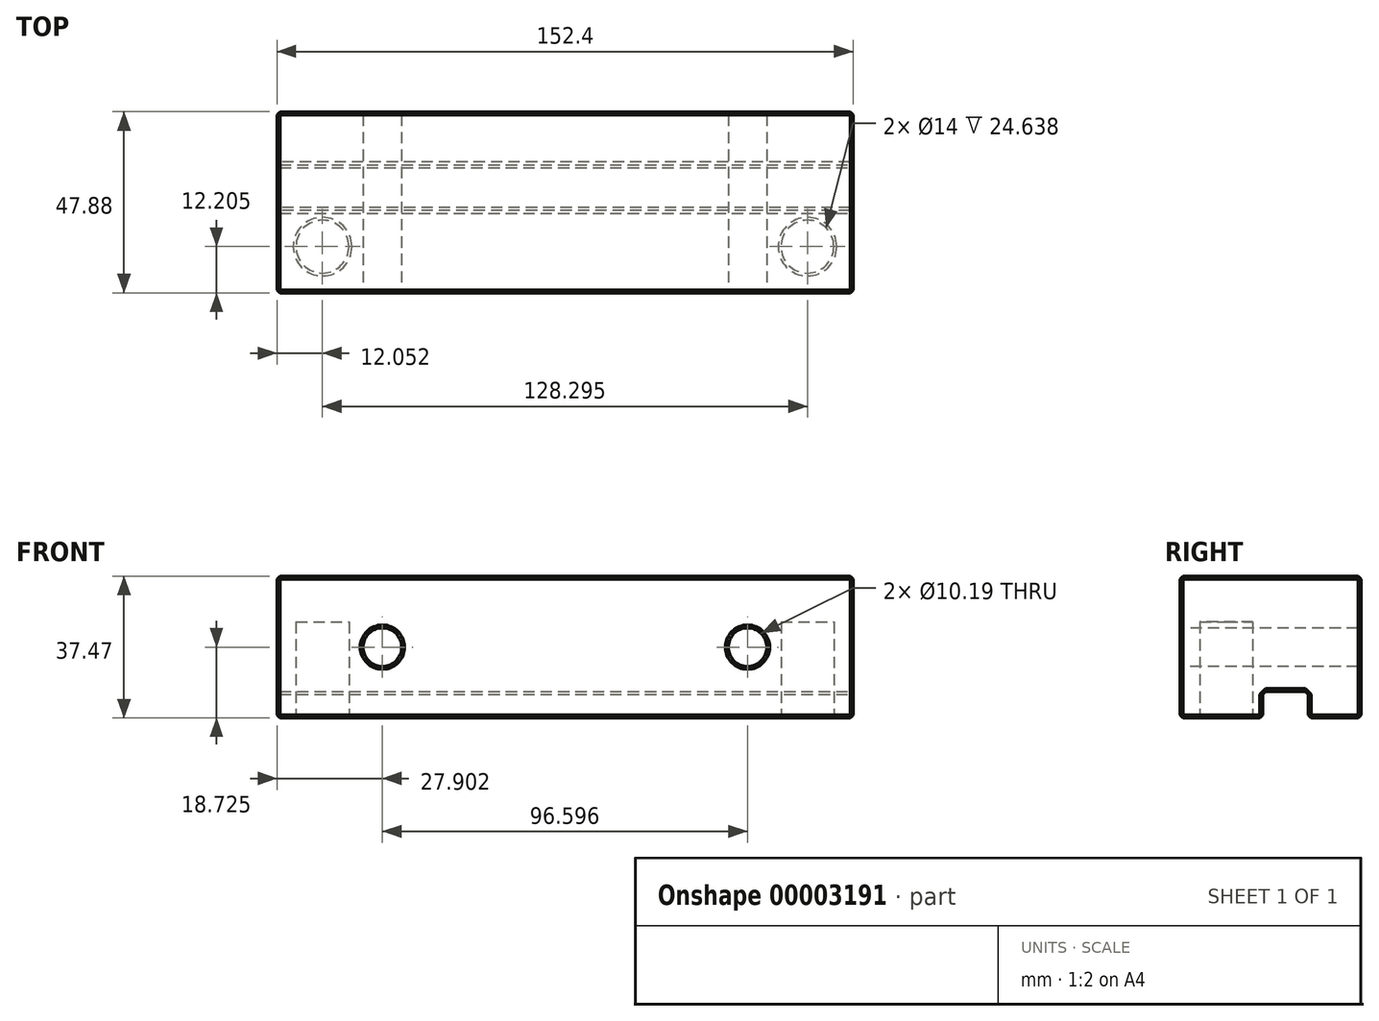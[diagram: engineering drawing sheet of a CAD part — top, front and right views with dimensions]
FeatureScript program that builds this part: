
annotation { "Feature Type Name" : "Feature", "Feature Type Description" : "" }
export const myFeature = defineFeature(function(context is Context, id is Id, definition is map)
    precondition{}
    {
        {
            var Q0;
            Q0=qCreatedBy(makeId("Front.planeOp"),FACE);
            var sketch = newSketch(context, id + "F0", { "sketchPlane" : qUnion([Q0])});
            skLineSegment(sketch, "E0.bottom", {"start": v(0, 0) * mm, "end": v(152.4, 0) * mm});
            skLineSegment(sketch, "E0.top", {"start": v(0, -37.47) * mm, "end": v(152.4, -37.47) * mm});
            skLineSegment(sketch, "E0.left", {"start": v(0, 0) * mm, "end": v(0, -37.47) * mm});
            skLineSegment(sketch, "E0.right", {"start": v(152.4, 0) * mm, "end": v(152.4, -37.47) * mm});
            skCircle(sketch, "E1", {"center": v(27.9, -18.75) * mm, "radius": 5.1 * mm});
            skCircle(sketch, "E2", {"center": v(124.5, -18.75) * mm, "radius": 5.1 * mm});
            skLineSegment(sketch, "E3", {"start": v(27.9, -18.75) * mm, "end": v(124.5, -18.75) * mm, "construction": true});
            skPoint(sketch, "E4", {"position": v(76.2, -18.75) * mm});
            skSolve(sketch);
        }
        {
            var Q0;
            Q0 = qSketchRegion(id + "F0", true);
            extrude(context, id + "F1", {"entities" : qUnion([Q0]), "oppositeDirection" : true, "depth" : 47.88 * mm});
        }
        {
            var Q0;
            Q0=makeQuery(id+"F1.opExtrude","SWEPT_FACE",FACE,{"disambiguationData":[OSD([sQuery(id+"F0.wireOp",EDGE,"E0.top")])]});
            var sketch = newSketch(context, id + "F2", { "sketchPlane" : qUnion([Q0])});
            skLineSegment(sketch, "E5.bottom", {"start": v(0, -21.8) * mm, "end": v(152.4, -21.8) * mm});
            skLineSegment(sketch, "E5.top", {"start": v(0, -33.86) * mm, "end": v(152.4, -33.86) * mm});
            skLineSegment(sketch, "E5.left", {"start": v(0, -21.8) * mm, "end": v(0, -33.86) * mm});
            skLineSegment(sketch, "E5.right", {"start": v(152.4, -21.8) * mm, "end": v(152.4, -33.86) * mm});
            skSolve(sketch);
        }
        {
            var Q0;
            Q0 = qSketchRegion(id + "F2", true);
            extrude(context, id + "F3", {"entities" : qUnion([Q0]), "operationType" : NewBodyOperationType.REMOVE, "oppositeDirection" : true, "depth" : 6.93 * mm});
        }
        {
            var Q0;
            {var subQ0=sQuery(id+"F0.wireOp",EDGE,"E0.top");Q0=makeQuery(id+"F3.boolean.opBoolean","SPLIT",FACE,{"disambiguationData":[TD([makeQuery(id+"F3.opExtrude","SWEPT_FACE",FACE,{"disambiguationData":[OSD([sQuery(id+"F2.wireOp",EDGE,"E5.bottom")])]})])],"derivedFrom":makeQuery(id+"F1.opExtrude","SWEPT_FACE",FACE,{"disambiguationData":[OSD([subQ0])]})});}
            var sketch = newSketch(context, id + "F4", { "sketchPlane" : qUnion([Q0])});
            skCircle(sketch, "E6", {"center": v(12.05, -12.2) * mm, "radius": 7 * mm});
            skCircle(sketch, "E7", {"center": v(140.35, -12.2) * mm, "radius": 7 * mm});
            skLineSegment(sketch, "E8", {"start": v(12.05, -12.2) * mm, "end": v(140.35, -12.2) * mm, "construction": true});
            skPoint(sketch, "E9", {"position": v(76.2, -12.2) * mm});
            skSolve(sketch);
        }
        {
            var Q0;
            Q0 = qSketchRegion(id + "F4", true);
            extrude(context, id + "F5", {"entities" : qUnion([Q0]), "operationType" : NewBodyOperationType.REMOVE, "oppositeDirection" : true, "depth" : 25.4 * mm});
        }
        {
            var Q0;
            {var subQ0=sQuery(id+"F0.wireOp",EDGE,"E0.top");Q0=makeQuery(id+"F3.boolean.opBoolean","SPLIT",FACE,{"disambiguationData":[TD([makeQuery(id+"F3.opExtrude","SWEPT_FACE",FACE,{"disambiguationData":[OSD([sQuery(id+"F2.wireOp",EDGE,"E5.bottom")])]})])],"derivedFrom":makeQuery(id+"F1.opExtrude","SWEPT_FACE",FACE,{"disambiguationData":[OSD([subQ0])]})});}
            var Q1;
            {var subQ0=sQuery(id+"F0.wireOp",EDGE,"E0.top");Q1=makeQuery(id+"F3.boolean.opBoolean","SPLIT",FACE,{"disambiguationData":[TD([makeQuery(id+"F3.opExtrude","SWEPT_FACE",FACE,{"disambiguationData":[OSD([sQuery(id+"F2.wireOp",EDGE,"E5.top")])]})])],"derivedFrom":makeQuery(id+"F1.opExtrude","SWEPT_FACE",FACE,{"disambiguationData":[OSD([subQ0])]})});}
            var Q2;
            Q2=makeQuery(id+"F3.boolean.opBoolean","COPY",FACE,{"derivedFrom":makeQuery(id+"F3.opExtrude","CAP_FACE",FACE,{"disambiguationData":[OSD([sQuery(id+"F2.wireOp",EDGE,"E5.bottom"),sQuery(id+"F2.wireOp",EDGE,"E5.top"),sQuery(id+"F2.wireOp",EDGE,"E5.left"),sQuery(id+"F2.wireOp",EDGE,"E5.right")])],"isStart":false})});
            var Q3;
            Q3=makeQuery(id+"F1.opExtrude","SWEPT_FACE",FACE,{"disambiguationData":[OSD([sQuery(id+"F0.wireOp",EDGE,"E0.left")])]});
            var Q4;
            Q4=makeQuery(id+"F1.opExtrude","CAP_FACE",FACE,{"disambiguationData":[OSD([sQuery(id+"F0.wireOp",EDGE,"E0.bottom"),sQuery(id+"F0.wireOp",EDGE,"E0.top"),sQuery(id+"F0.wireOp",EDGE,"E0.left"),sQuery(id+"F0.wireOp",EDGE,"E0.right"),sQuery(id+"F0.wireOp",EDGE,"E1"),sQuery(id+"F0.wireOp",EDGE,"E2")])],"isStart":false});
            var Q5;
            Q5=makeQuery(id+"F1.opExtrude","SWEPT_FACE",FACE,{"disambiguationData":[OSD([sQuery(id+"F0.wireOp",EDGE,"E0.bottom")])]});
            var Q6;
            Q6=makeQuery(id+"F1.opExtrude","CAP_FACE",FACE,{"disambiguationData":[OSD([sQuery(id+"F0.wireOp",EDGE,"E0.bottom"),sQuery(id+"F0.wireOp",EDGE,"E0.top"),sQuery(id+"F0.wireOp",EDGE,"E0.left"),sQuery(id+"F0.wireOp",EDGE,"E0.right"),sQuery(id+"F0.wireOp",EDGE,"E1"),sQuery(id+"F0.wireOp",EDGE,"E2")])],"isStart":true});
            chamfer(context, id + "F6", {"entities" : qUnion([Q0, Q1, Q2, Q3, Q4, Q5, Q6]), "width" : 0.76 * mm, "tangentPropagation" : true});
        }
    });
